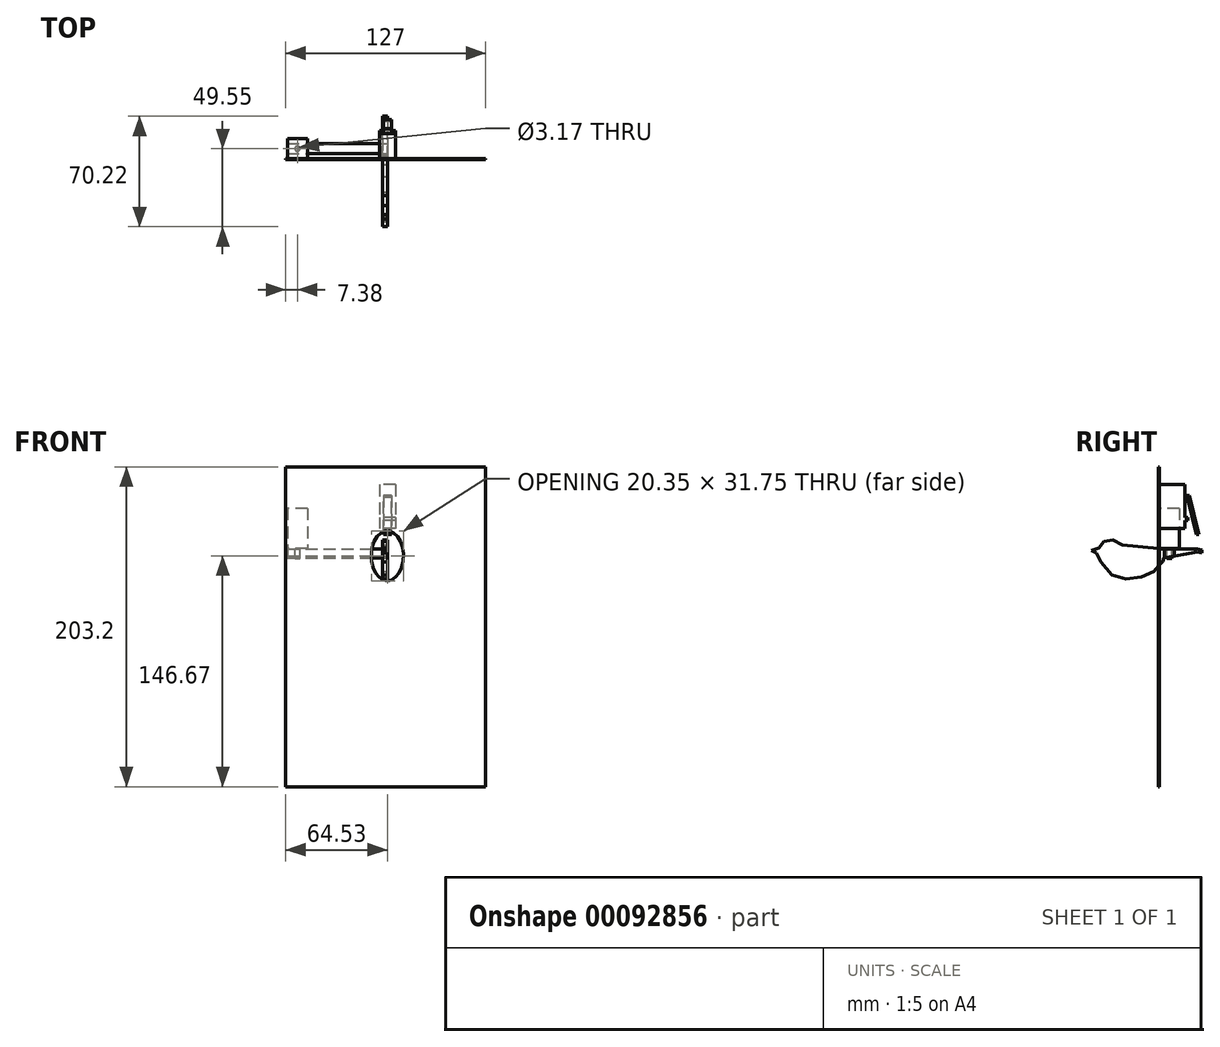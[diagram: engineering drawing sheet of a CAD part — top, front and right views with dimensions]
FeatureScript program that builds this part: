
annotation { "Feature Type Name" : "Feature", "Feature Type Description" : "" }
export const myFeature = defineFeature(function(context is Context, id is Id, definition is map)
    precondition{}
    {
        {
            var Q0;
            Q0=qCreatedBy(makeId("Front.planeOp"),FACE);
            var sketch = newSketch(context, id + "F0", { "sketchPlane" : qUnion([Q0])});
            skLineSegment(sketch, "E0.bottom", {"start": v(-64.53, 88.28) * mm, "end": v(62.47, 88.28) * mm});
            skLineSegment(sketch, "E0.top", {"start": v(-64.53, -114.92) * mm, "end": v(62.47, -114.92) * mm});
            skLineSegment(sketch, "E0.left", {"start": v(-64.53, 88.28) * mm, "end": v(-64.53, -114.92) * mm});
            skLineSegment(sketch, "E0.right", {"start": v(62.47, 88.28) * mm, "end": v(62.47, -114.92) * mm});
            skEllipse(sketch, "E1", {"center": v(0, 31.75) * mm, "majorRadius": 15.88 * mm, "minorRadius": 10.18 * mm, "majorAxis": v(0, -1)});
            skSolve(sketch);
        }
        {
            assignVariable(context, id + "F1", {"name" : "BoardWidth", "anyValue" : .625});
        }
        {
            var Q0;
            Q0=qCreatedBy(makeId("Right.planeOp"),FACE);
            var sketch = newSketch(context, id + "F2", { "sketchPlane" : qUnion([Q0])});
            skLineSegment(sketch, "E2", {"start": v(-43.2, 35.26) * mm, "end": v(-38.32, 36.87) * mm});
            skLineSegment(sketch, "E3", {"start": v(-35.33, 40.71) * mm, "end": v(-38.32, 36.87) * mm});
            skLineSegment(sketch, "E4", {"start": v(-35.33, 40.71) * mm, "end": v(-29.62, 41.82) * mm});
            skLineSegment(sketch, "E5", {"start": v(-29.62, 41.82) * mm, "end": v(-23.48, 38.5) * mm});
            skLineSegment(sketch, "E6", {"start": v(-23.48, 38.5) * mm, "end": v(0.6, 36.25) * mm});
            skLineSegment(sketch, "E7", {"start": v(0.6, 36.25) * mm, "end": v(14.27, 36.25) * mm});
            skLineSegment(sketch, "E8", {"start": v(27.02, 35.43) * mm, "end": v(24.22, 36.25) * mm});
            skLineSegment(sketch, "E9", {"start": v(27.02, 35.43) * mm, "end": v(27.02, 33.47) * mm});
            skLineSegment(sketch, "E10", {"start": v(27.02, 33.47) * mm, "end": v(24.16, 34.14) * mm});
            skLineSegment(sketch, "E11", {"start": v(24.16, 34.14) * mm, "end": v(19.93, 33.4) * mm});
            skLineSegment(sketch, "E12", {"start": v(2.96, 30.4) * mm, "end": v(2.02, 28.09) * mm});
            skLineSegment(sketch, "E13", {"start": v(2.02, 28.09) * mm, "end": v(-3.7, 21.86) * mm});
            skLineSegment(sketch, "E14", {"start": v(-3.7, 21.86) * mm, "end": v(-11.45, 18.28) * mm});
            skLineSegment(sketch, "E15", {"start": v(-11.45, 18.28) * mm, "end": v(-21.26, 17) * mm});
            skLineSegment(sketch, "E16", {"start": v(-21.26, 17) * mm, "end": v(-30.13, 19.63) * mm});
            skLineSegment(sketch, "E17", {"start": v(-30.13, 19.63) * mm, "end": v(-37.2, 27.75) * mm});
            skLineSegment(sketch, "E18", {"start": v(-37.2, 27.75) * mm, "end": v(-40.02, 33.55) * mm});
            skLineSegment(sketch, "E19", {"start": v(-40.02, 33.55) * mm, "end": v(-43.2, 35.26) * mm});
            skLineSegment(sketch, "E20.trimOffspring", {"start": v(19.92, 36.25) * mm, "end": v(24.22, 36.25) * mm});
            skLineSegment(sketch, "E21.trimOffspring", {"start": v(14.7, 32.47) * mm, "end": v(2.96, 30.4) * mm});
            skLineSegment(sketch, "E22", {"start": v(19.92, 36.25) * mm, "end": v(14.27, 36.25) * mm});
            skLineSegment(sketch, "E23", {"start": v(19.93, 33.4) * mm, "end": v(14.7, 32.47) * mm});
            skSolve(sketch);
        }
        {
            var Q0;
            Q0=qSketchRegion(id+"F2",true);
            extrude(context, id + "F3", {"entities" : qUnion([Q0]), "oppositeDirection" : true, "depth" : 3.17 * mm});
        }
        {
            var Q0;
            Q0=qSketchRegion(id+"F0",true);
            extrude(context, id + "F4", {"entities" : qUnion([Q0]), "depth" : (getVariable(context, 'BoardWidth')) * mm});
        }
        {
            var Q0;
            Q0=makeQuery(id+"F4.opExtrude","SWEPT_FACE",FACE,{"disambiguationData":[OSD([sQuery(id+"F0.wireOp",EDGE,"E0.right")])]});
            var sketch = newSketch(context, id + "F5", { "sketchPlane" : qUnion([Q0])});
            skLineSegment(sketch, "E24.bottom", {"start": v(-15.88, 88.28) * mm, "end": v(111.12, 88.28) * mm});
            skLineSegment(sketch, "E24.top", {"start": v(-15.88, -114.92) * mm, "end": v(111.12, -114.92) * mm});
            skLineSegment(sketch, "E24.left", {"start": v(-15.88, 88.28) * mm, "end": v(-15.88, -114.92) * mm});
            skLineSegment(sketch, "E24.right", {"start": v(111.12, 88.28) * mm, "end": v(111.12, -114.92) * mm});
            skSolve(sketch);
        }
        {
            var Q0;
            Q0=qCreatedBy(makeId("Right.planeOp"),FACE);
            var sketch = newSketch(context, id + "F6", { "sketchPlane" : qUnion([Q0])});
            skLineSegment(sketch, "E25.bottom", {"start": v(16, 77.05) * mm, "end": v(0, 77.05) * mm});
            skLineSegment(sketch, "E25.top", {"start": v(16, 49.05) * mm, "end": v(0, 49.05) * mm});
            skLineSegment(sketch, "E25.left", {"start": v(16, 77.05) * mm, "end": v(16, 49.05) * mm});
            skLineSegment(sketch, "E25.right", {"start": v(0, 77.05) * mm, "end": v(0, 49.05) * mm});
            skLineSegment(sketch, "E26", {"start": v(16, 56.2) * mm, "end": v(18, 56.2) * mm});
            skLineSegment(sketch, "E27", {"start": v(18, 56.2) * mm, "end": v(18, 54.1) * mm});
            skLineSegment(sketch, "E28", {"start": v(18, 54.1) * mm, "end": v(16, 54.1) * mm});
            skPoint(sketch, "E29.endSnap0", {"position": v(18, 55.15) * mm});
            skLineSegment(sketch, "E30", {"start": v(16, 56.2) * mm, "end": v(18, 54.1) * mm, "construction": true});
            skLineSegment(sketch, "E31", {"start": v(18, 56.2) * mm, "end": v(16, 54.1) * mm, "construction": true});
            skSolve(sketch);
        }
        {
            var Q0;
            Q0=qSketchRegion(id+"F6",true);
            extrude(context, id + "F7", {"entities" : qUnion([Q0]), "depth" : 5.1 * mm, "hasSecondDirection" : true, "secondDirectionOppositeDirection" : true, "secondDirectionDepth" : 5.1 * mm});
        }
        {
            var Q0;
            Q0=qCreatedBy(makeId("Right.planeOp"),FACE);
            var sketch = newSketch(context, id + "F8", { "sketchPlane" : qUnion([Q0])});
            skLineSegment(sketch, "E32", {"start": v(16, 69.96) * mm, "end": v(16, 68.83) * mm});
            skLineSegment(sketch, "E33", {"start": v(16, 69.96) * mm, "end": v(19, 69.96) * mm});
            skLineSegment(sketch, "E34", {"start": v(19, 69.96) * mm, "end": v(25, 45.24) * mm});
            skLineSegment(sketch, "E35", {"start": v(23.48, 45.24) * mm, "end": v(25, 45.24) * mm});
            skLineSegment(sketch, "E36", {"start": v(23.48, 45.24) * mm, "end": v(17.76, 68.81) * mm});
            skLineSegment(sketch, "E37", {"start": v(16, 68.83) * mm, "end": v(17.76, 68.81) * mm});
            skSolve(sketch);
        }
        {
            var Q0;
            Q0=qSketchRegion(id+"F8",true);
            extrude(context, id + "F9", {"entities" : qUnion([Q0]), "operationType" : NewBodyOperationType.ADD, "depth" : 2.5 * mm, "hasSecondDirection" : true, "secondDirectionOppositeDirection" : true, "secondDirectionDepth" : 2.5 * mm});
        }
        {
            var Q0;
            Q0=qCreatedBy(makeId("Front.planeOp"),FACE);
            var sketch = newSketch(context, id + "F10", { "sketchPlane" : qUnion([Q0])});
            skLineSegment(sketch, "E38.bottom", {"start": v(-4.76, -3.36) * mm, "end": v(-43.52, -3.36) * mm});
            skLineSegment(sketch, "E38.top", {"start": v(-4.76, -37.37) * mm, "end": v(-43.52, -37.37) * mm});
            skLineSegment(sketch, "E38.left", {"start": v(-4.76, -3.36) * mm, "end": v(-4.76, -37.37) * mm});
            skLineSegment(sketch, "E38.right", {"start": v(-43.52, -3.36) * mm, "end": v(-43.52, -37.37) * mm});
            skSolve(sketch);
        }
        {
            var Q0;
            Q0=makeQuery(id+"F4.opExtrude","CAP_FACE",FACE,{"disambiguationData":[OSD([sQuery(id+"F0.wireOp",EDGE,"E0.bottom"),sQuery(id+"F0.wireOp",EDGE,"E0.top"),sQuery(id+"F0.wireOp",EDGE,"E0.left"),sQuery(id+"F0.wireOp",EDGE,"E0.right"),sQuery(id+"F0.wireOp",EDGE,"E1")])],"isStart":true});
            var sketch = newSketch(context, id + "F11", { "sketchPlane" : qUnion([Q0])});
            skLineSegment(sketch, "E39", {"start": v(0, 47.62) * mm, "end": v(0, 15.88) * mm, "construction": true});
            skLineSegment(sketch, "E40", {"start": v(0, 31.75) * mm, "end": v(62.48, 31.75) * mm, "construction": true});
            skLineSegment(sketch, "E41.bottom", {"start": v(50.8, 61.91) * mm, "end": v(63.5, 61.91) * mm});
            skLineSegment(sketch, "E41.top", {"start": v(50.8, 36.51) * mm, "end": v(63.5, 36.51) * mm});
            skLineSegment(sketch, "E41.left", {"start": v(50.8, 61.91) * mm, "end": v(50.8, 36.51) * mm});
            skLineSegment(sketch, "E41.right", {"start": v(63.5, 61.91) * mm, "end": v(63.5, 36.51) * mm});
            skSolve(sketch);
        }
        {
            var Q0;
            Q0 = qSketchRegion(id + "F11", true);
            extrude(context, id + "F12", {"entities" : qUnion([Q0]), "depth" : 12.7 * mm});
        }
        {
            var Q0;
            Q0=makeQuery(id+"F12.opExtrude","SWEPT_FACE",FACE,{"disambiguationData":[OSD([sQuery(id+"F11.wireOp",EDGE,"E41.top")])]});
            var sketch = newSketch(context, id + "F13", { "sketchPlane" : qUnion([Q0])});
            skCircle(sketch, "E42", {"center": v(-57.15, -6.35) * mm, "radius": 1.59 * mm});
            skSolve(sketch);
        }
        {
            var Q0;
            Q0 = qSketchRegion(id + "F13", true);
            extrude(context, id + "F14", {"entities" : qUnion([Q0]), "depth" : 6.35 * mm});
        }
        {
            var Q0;
            Q0=makeQuery(id+"F3.opExtrude","CAP_FACE",FACE,{"disambiguationData":[OSD([sQuery(id+"F2.wireOp",EDGE,"E2"),sQuery(id+"F2.wireOp",EDGE,"E3"),sQuery(id+"F2.wireOp",EDGE,"E4"),sQuery(id+"F2.wireOp",EDGE,"E5"),sQuery(id+"F2.wireOp",EDGE,"E6"),sQuery(id+"F2.wireOp",EDGE,"E7"),sQuery(id+"F2.wireOp",EDGE,"E8"),sQuery(id+"F2.wireOp",EDGE,"E9"),sQuery(id+"F2.wireOp",EDGE,"E10"),sQuery(id+"F2.wireOp",EDGE,"E11"),sQuery(id+"F2.wireOp",EDGE,"E12"),sQuery(id+"F2.wireOp",EDGE,"E13"),sQuery(id+"F2.wireOp",EDGE,"E14"),sQuery(id+"F2.wireOp",EDGE,"E15"),sQuery(id+"F2.wireOp",EDGE,"E16"),sQuery(id+"F2.wireOp",EDGE,"E17"),sQuery(id+"F2.wireOp",EDGE,"E18"),sQuery(id+"F2.wireOp",EDGE,"E19"),sQuery(id+"F2.wireOp",EDGE,"E20.trimOffspring"),sQuery(id+"F2.wireOp",EDGE,"E21.trimOffspring"),sQuery(id+"F2.wireOp",EDGE,"E22"),sQuery(id+"F2.wireOp",EDGE,"E23")])],"isStart":true});
            var sketch = newSketch(context, id + "F15", { "sketchPlane" : qUnion([Q0])});
            skLineSegment(sketch, "E43", {"start": v(9.53, 36.25) * mm, "end": v(3.17, 36.25) * mm});
            skLineSegment(sketch, "E44", {"start": v(3.18, 30.43) * mm, "end": v(3.17, 36.25) * mm});
            skLineSegment(sketch, "E45", {"start": v(9.53, 36.25) * mm, "end": v(9.53, 31.55) * mm});
            skLineSegment(sketch, "E46", {"start": v(3.18, 30.43) * mm, "end": v(9.53, 31.55) * mm});
            skSolve(sketch);
        }
        {
            var Q0;
            Q0 = qSketchRegion(id + "F15", true);
            extrude(context, id + "F16", {"entities" : qUnion([Q0]), "oppositeDirection" : true, "depth" : 63.5 * mm});
        }
        {
            var Q0;
            Q0=makeQuery(id+"F14.opExtrude","SWEPT_BODY",BODY,{"disambiguationData":[OSD([sQuery(id+"F13.wireOp",EDGE,"E42")])]});
            var Q1;
            Q1=makeQuery(id+"F16.opExtrude","SWEPT_BODY",BODY,{"disambiguationData":[OSD([sQuery(id+"F15.wireOp",EDGE,"E43"),sQuery(id+"F15.wireOp",EDGE,"E44"),sQuery(id+"F15.wireOp",EDGE,"E45"),sQuery(id+"F15.wireOp",EDGE,"E46")])]});
            booleanBodies(context, id + "F17", {"operationType" : BooleanOperationType.SUBTRACTION, "tools" : qUnion([Q0]), "targets" : qUnion([Q1]), "keepTools" : true});
        }
    });
